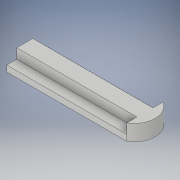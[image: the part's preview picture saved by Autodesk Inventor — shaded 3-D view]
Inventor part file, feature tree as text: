
AUTODESK INVENTOR PART (.ipt)
format: ipt  version: 2019 (Build 230136000, 136)  size: 111,104 bytes
history: native  units: in
note: dims shown in document units (in); Inventor stores cm internally (conversion verified against a paired STEP export)
features: extrude x2, sketch x2
ambient origin geometry x8: Origin, YZ Plane, XZ Plane, XY Plane, X Axis, Y Axis, Z Axis, Center Point
bodies: Solid1 (feature_tree)
feature tree (4):
  extrude  "Extrusion1"  Depth=0.1in
  extrude  "Extrusion2"  Depth=0.038in
  sketch  "Sketch1"  dims[d0=0.225in d1=0.1in]
  sketch  "Sketch2"  dims[d2=0.0625in d3=0.038in d4=0.062in d5=0.75in d6=0.0in d7=0.75in d8=0.0in]
